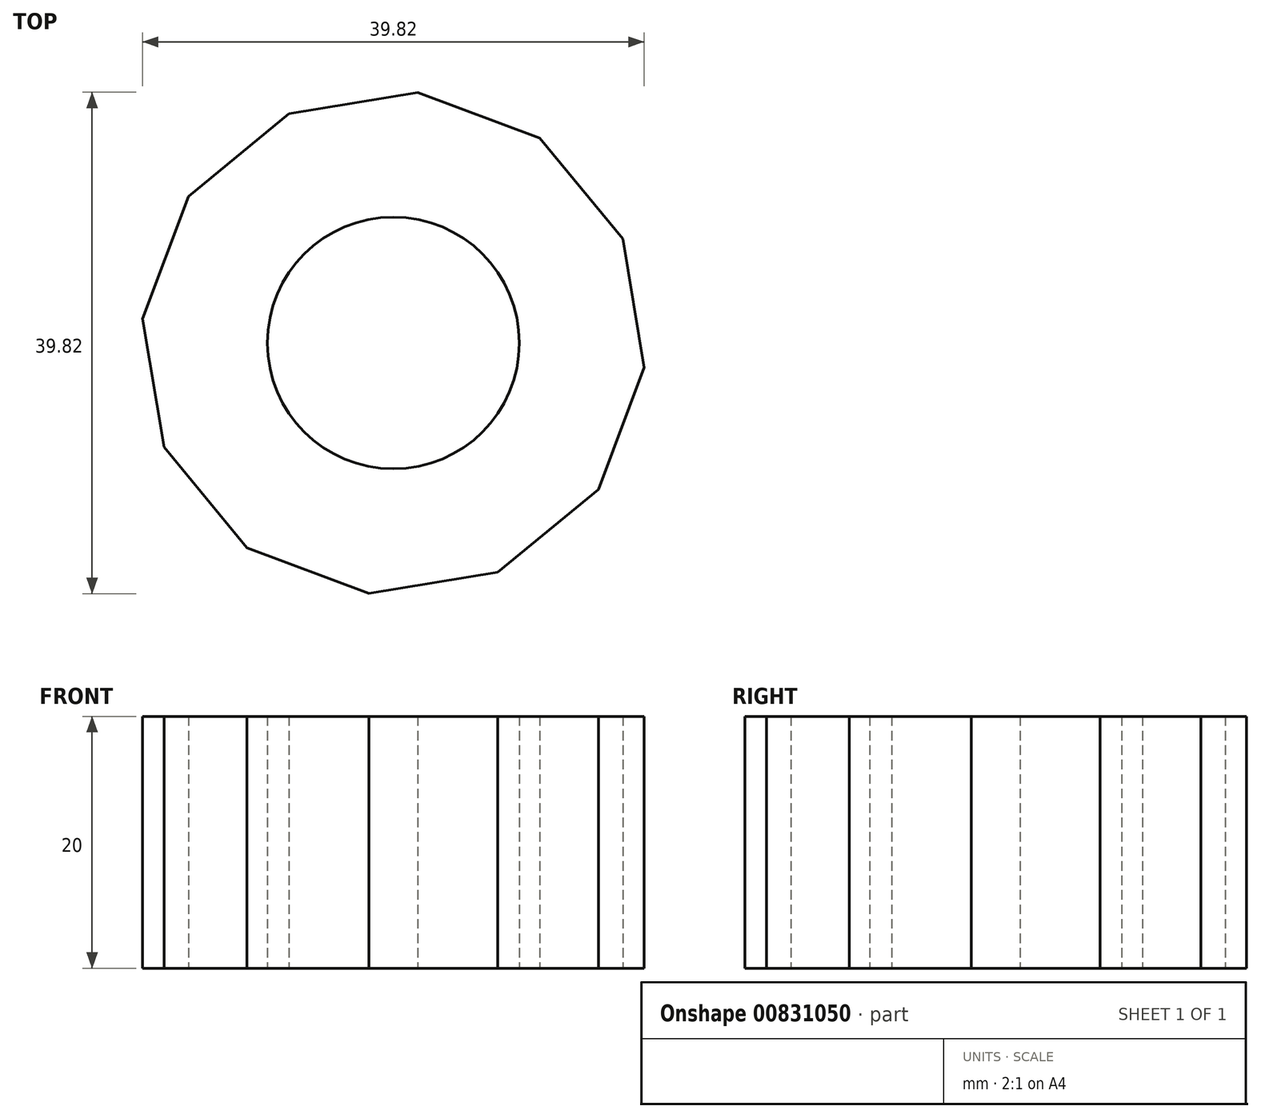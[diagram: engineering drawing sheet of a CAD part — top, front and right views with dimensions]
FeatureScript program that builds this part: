
annotation { "Feature Type Name" : "Feature", "Feature Type Description" : "" }
export const myFeature = defineFeature(function(context is Context, id is Id, definition is map)
    precondition{}
    {
        {
            var Q0;
            Q0=qCreatedBy(makeId("Top.planeOp"),FACE);
            var sketch = newSketch(context, id + "F0", { "sketchPlane" : qUnion([Q0])});
            skCircle(sketch, "E0", {"center": v(0, 0) * mm, "radius": 20 * mm});
            skCircle(sketch, "E1", {"center": v(0, 0) * mm, "radius": 10 * mm});
            skCircle(sketch, "E2.cCircle", {"center": v(0, 0) * mm, "radius": 20 * mm, "construction": true});
            skLineSegment(sketch, "E2.0", {"start": v(11.63, 16.27) * mm, "end": v(18.2, 8.28) * mm});
            skLineSegment(sketch, "E2.1", {"start": v(18.2, 8.28) * mm, "end": v(19.9, -1.94) * mm});
            skLineSegment(sketch, "E2.2", {"start": v(19.9, -1.94) * mm, "end": v(16.27, -11.63) * mm});
            skLineSegment(sketch, "E2.3", {"start": v(16.27, -11.63) * mm, "end": v(8.28, -18.2) * mm});
            skLineSegment(sketch, "E2.4", {"start": v(8.28, -18.2) * mm, "end": v(-1.94, -19.9) * mm});
            skLineSegment(sketch, "E2.5", {"start": v(-1.94, -19.9) * mm, "end": v(-11.63, -16.27) * mm});
            skLineSegment(sketch, "E2.6", {"start": v(-11.63, -16.27) * mm, "end": v(-18.2, -8.28) * mm});
            skLineSegment(sketch, "E2.7", {"start": v(-18.2, -8.28) * mm, "end": v(-19.9, 1.94) * mm});
            skLineSegment(sketch, "E2.8", {"start": v(-19.9, 1.94) * mm, "end": v(-16.27, 11.63) * mm});
            skLineSegment(sketch, "E2.9", {"start": v(-16.27, 11.63) * mm, "end": v(-8.28, 18.2) * mm});
            skLineSegment(sketch, "E2.10", {"start": v(-8.28, 18.2) * mm, "end": v(1.94, 19.9) * mm});
            skLineSegment(sketch, "E2.11", {"start": v(1.94, 19.9) * mm, "end": v(11.63, 16.27) * mm});
            skSolve(sketch);
        }
        {
            var Q0;
            Q0=makeQuery(id+"F0.imprint","IMPRINT",FACE,{"disambiguationData":[TD([[makeQuery(id+"F0.imprint","IMPRINT",EDGE,{"derivedFrom":sQuery(id+"F0.wireOp",EDGE,"E1")}),-1.0]])]});
            extrude(context, id + "F1", {"entities" : qUnion([Q0]), "depth" : 20 * mm, "offsetDistance" : 25 * mm});
        }
    });
